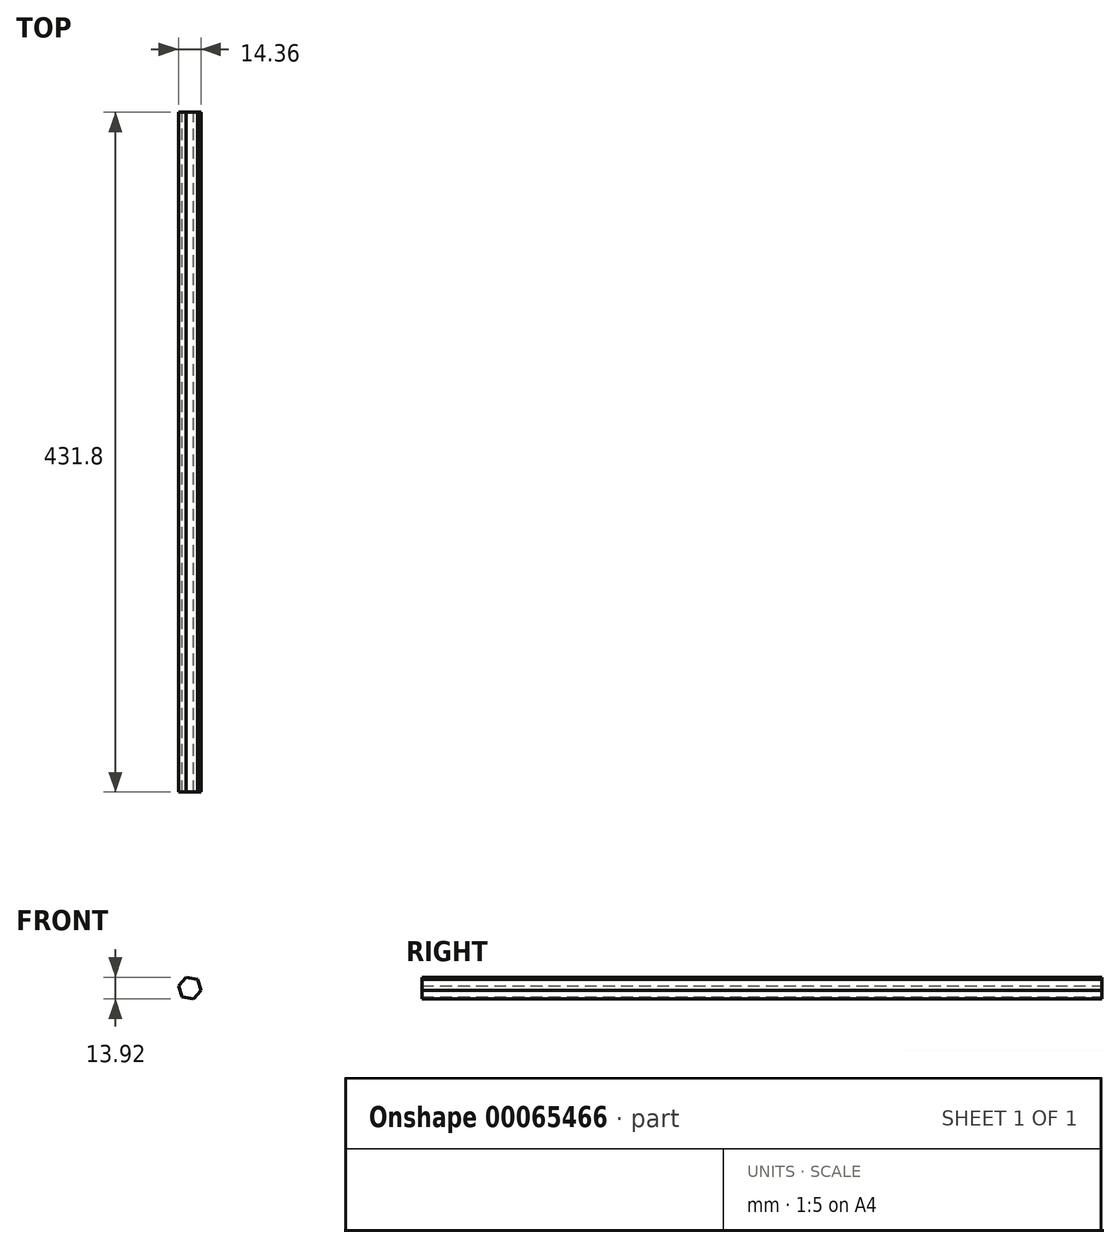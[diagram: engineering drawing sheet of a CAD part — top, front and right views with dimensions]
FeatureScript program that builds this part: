
annotation { "Feature Type Name" : "Feature", "Feature Type Description" : "" }
export const myFeature = defineFeature(function(context is Context, id is Id, definition is map)
    precondition{}
    {
        {
            var Q0;
            Q0=qCreatedBy(makeId("Front.planeOp"),FACE);
            var sketch = newSketch(context, id + "F0", { "sketchPlane" : qUnion([Q0])});
            skCircle(sketch, "E0.cCircle", {"center": v(0, 0) * mm, "radius": 6.35 * mm, "construction": true});
            skLineSegment(sketch, "E0.0", {"start": v(4.88, 5.47) * mm, "end": v(7.18, -1.5) * mm});
            skLineSegment(sketch, "E0.1", {"start": v(7.18, -1.5) * mm, "end": v(2.3, -6.96) * mm});
            skLineSegment(sketch, "E0.2", {"start": v(2.3, -6.96) * mm, "end": v(-4.88, -5.47) * mm});
            skLineSegment(sketch, "E0.3", {"start": v(-4.88, -5.47) * mm, "end": v(-7.18, 1.5) * mm});
            skLineSegment(sketch, "E0.4", {"start": v(-7.18, 1.5) * mm, "end": v(-2.3, 6.96) * mm});
            skLineSegment(sketch, "E0.5", {"start": v(-2.3, 6.96) * mm, "end": v(4.88, 5.47) * mm});
            skPoint(sketch, "E0.0.midPoint", {"position": v(6.03, 1.99) * mm});
            skSolve(sketch);
        }
        {
            var Q0;
            Q0=makeQuery(id+"F0.imprint","IMPRINT",FACE,{"disambiguationData":[TD([[makeQuery(id+"F0.imprint","IMPRINT",EDGE,{"derivedFrom":sQuery(id+"F0.wireOp",EDGE,"E0.0")}),-1.0]])]});
            extrude(context, id + "F1", {"entities" : qUnion([Q0]), "depth" : 431.8 * mm});
        }
    });
